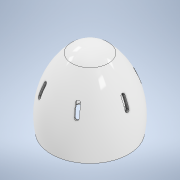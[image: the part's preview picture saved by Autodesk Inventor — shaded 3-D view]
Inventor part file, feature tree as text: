
AUTODESK INVENTOR PART (.ipt)
format: ipt  version: 2020 (Build 240168000, 168)  size: 473,600 bytes
history: native  units: in
note: dims shown in document units (in); Inventor stores cm internally (conversion verified against a paired STEP export)
features: other x5, revolve x4, helix x2, boolean_combine x2, thread x2, extrude x1, pattern_circular x1, shell x1, sketch x1
ambient origin geometry x8: Origin, YZ Plane, XZ Plane, XY Plane, X Axis, Y Axis, Z Axis, Center Point
bodies: Solid1 (feature_tree), Solid2 (feature_tree), Solid3 (feature_tree)
feature tree (19):
  other  "SmartEgg Shell.ipt"
  revolve  "Revolution1"  Angle=90.0deg
  helix  "Coil1"  [1 undecoded]
  helix  "Coil2"  [1 undecoded]
  revolve  "Revolution2"  Angle=90.0deg
  other  "Extra Cutout"
  revolve  "Revolution3"  [1 undecoded]
  boolean_combine  "Combine1"
  extrude  "Extrusion1"  Depth=0.1969in
  pattern_circular  "Circular Pattern1"  [2 undecoded]
  boolean_combine  "Combine2"
  revolve  "Revolution4"  Angle=360.0deg
  shell  "Shell Sketch"  Thickness=90.0deg
  thread  "Thread Sketch"  [1 undecoded]
  thread  "Thread Mask"  [1 undecoded]
  other  "Top Thread Mask"
  other  "Vent Plane"
  sketch  "Sketch6"  dims[d0=0.3937in d1=90.0deg d2=0.3706in d3=1.0in d4=1.1811in d5=0.0in d6=90.0deg d7=90.0deg d8=0.0in d9=0.0in d10=0.3706in d11=1.0in d12=1.1811in d13=0.0in d14=90.0deg d15=90.0deg d16=0.0in d17=0.0in d18=90.0deg d19=0.0984in d20=0.2953in d21=0.3937in d22=0.0in d23=2.3622in d24=360.0deg d30=90.0deg d32=0.1969in d33=90.0deg d34=0.0098in d31=0.0344in]
  other  "Vent Lookup"
note: 7 required parameter values undecoded (feature->parameter linkage not recoverable at this tier; creation-order binding heuristic only, values carry confidence <= 0.55)